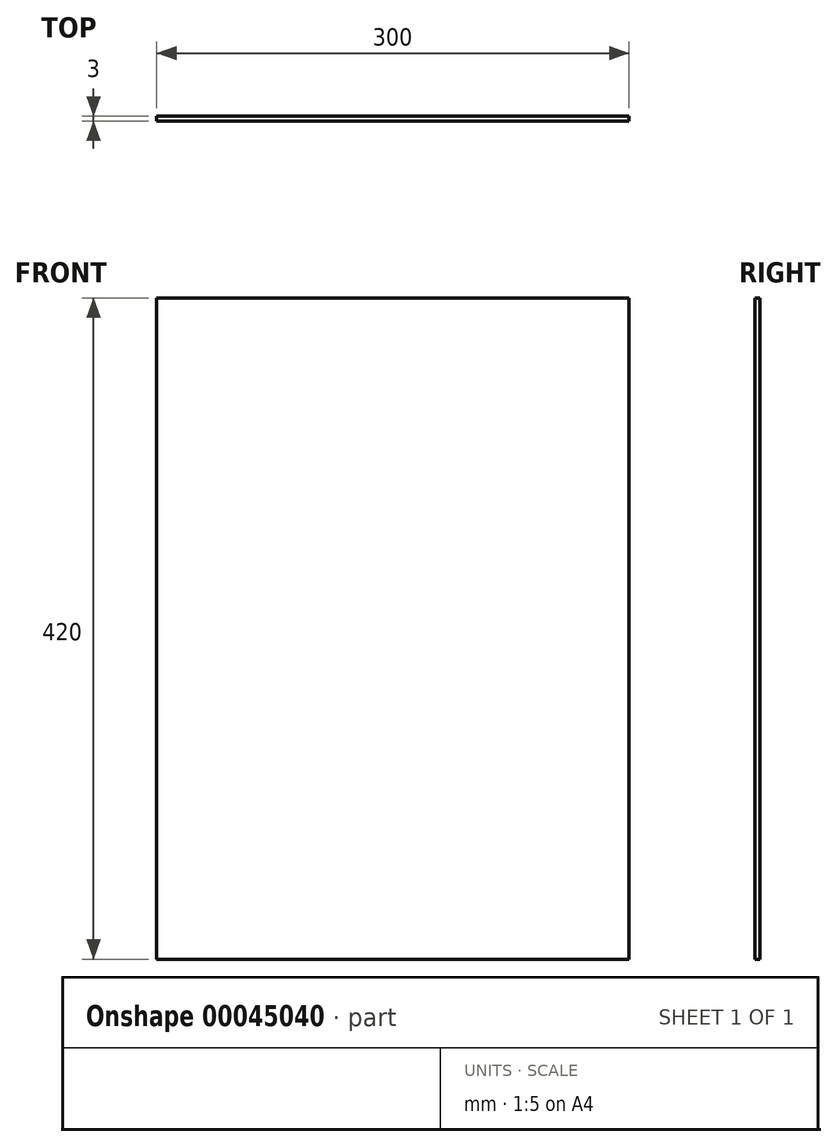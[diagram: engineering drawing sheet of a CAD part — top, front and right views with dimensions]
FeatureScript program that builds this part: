
annotation { "Feature Type Name" : "Feature", "Feature Type Description" : "" }
export const myFeature = defineFeature(function(context is Context, id is Id, definition is map)
    precondition{}
    {
        {
            var Q0;
            Q0=qCreatedBy(makeId("Front.planeOp"),FACE);
            var sketch = newSketch(context, id + "F0", { "sketchPlane" : qUnion([Q0])});
            skLineSegment(sketch, "E0.bottom", {"start": v(0, 0) * mm, "end": v(300, 0) * mm});
            skLineSegment(sketch, "E0.top", {"start": v(0, 420) * mm, "end": v(300, 420) * mm});
            skLineSegment(sketch, "E0.left", {"start": v(0, 0) * mm, "end": v(0, 420) * mm});
            skLineSegment(sketch, "E0.right", {"start": v(300, 0) * mm, "end": v(300, 420) * mm});
            skSolve(sketch);
        }
        {
            var Q0;
            Q0 = qSketchRegion(id + "F0", true);
            extrude(context, id + "F1", {"entities" : qUnion([Q0]), "depth" : 3 * mm});
        }
    });
